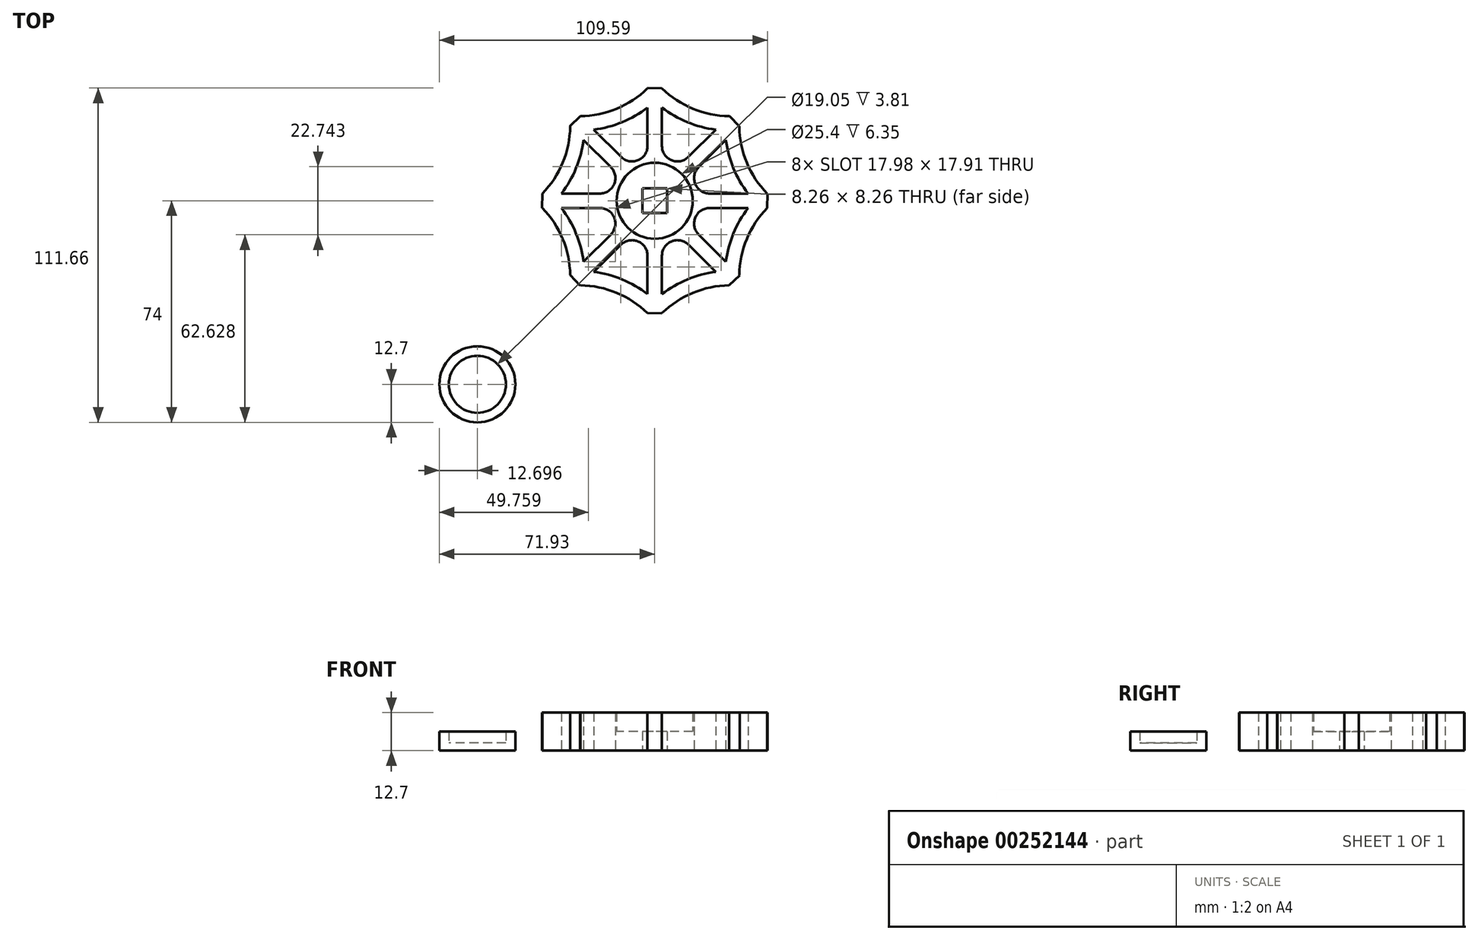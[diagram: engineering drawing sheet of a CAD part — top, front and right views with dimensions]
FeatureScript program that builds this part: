
annotation { "Feature Type Name" : "Feature", "Feature Type Description" : "" }
export const myFeature = defineFeature(function(context is Context, id is Id, definition is map)
    precondition{}
    {
        {
            var Q0;
            Q0=qCreatedBy(makeId("Top.planeOp"),FACE);
            var sketch = newSketch(context, id + "F0", { "sketchPlane" : qUnion([Q0])});
            skCircle(sketch, "E0", {"center": v(0, 0) * mm, "radius": 12.7 * mm});
            skLineSegment(sketch, "E1.0", {"start": v(18.33, -2.42) * mm, "end": v(37.66, -2.42) * mm});
            skLineSegment(sketch, "E2.0", {"start": v(18.33, 2.42) * mm, "end": v(37.66, 2.42) * mm});
            skLineSegment(sketch, "E3.trimOffspring", {"start": v(38.59, 2.42) * mm, "end": v(38.67, 2.42) * mm});
            skLineSegment(sketch, "E4.trimOffspring", {"start": v(38.59, -2.42) * mm, "end": v(38.67, -2.42) * mm});
            skLineSegment(sketch, "E5.1.0", {"start": v(11.25, 14.67) * mm, "end": v(24.92, 28.34) * mm});
            skLineSegment(sketch, "E5.1.1", {"start": v(14.67, 11.25) * mm, "end": v(28.34, 24.92) * mm});
            skLineSegment(sketch, "E5.2.0", {"start": v(-2.42, 18.33) * mm, "end": v(-2.42, 37.66) * mm});
            skLineSegment(sketch, "E5.2.1", {"start": v(2.42, 18.33) * mm, "end": v(2.42, 37.66) * mm});
            skLineSegment(sketch, "E6.3.3.0", {"start": v(-11.25, 14.67) * mm, "end": v(-24.92, 28.34) * mm});
            skLineSegment(sketch, "E6.4.3.0", {"start": v(-14.67, 11.25) * mm, "end": v(-28.34, 24.92) * mm});
            skLineSegment(sketch, "E6.3.4.0", {"start": v(-18.33, 2.42) * mm, "end": v(-37.66, 2.42) * mm});
            skLineSegment(sketch, "E6.4.4.0", {"start": v(-18.33, -2.42) * mm, "end": v(-37.66, -2.42) * mm});
            skLineSegment(sketch, "E6.3.5.0", {"start": v(-14.67, -11.25) * mm, "end": v(-28.34, -24.92) * mm});
            skLineSegment(sketch, "E6.4.5.0", {"start": v(-11.25, -14.67) * mm, "end": v(-24.92, -28.34) * mm});
            skLineSegment(sketch, "E6.3.6.0", {"start": v(-2.42, -18.33) * mm, "end": v(-2.42, -37.66) * mm});
            skLineSegment(sketch, "E6.4.6.0", {"start": v(2.42, -18.33) * mm, "end": v(2.42, -37.66) * mm});
            skLineSegment(sketch, "E6.3.7.0", {"start": v(11.25, -14.67) * mm, "end": v(24.92, -28.34) * mm});
            skLineSegment(sketch, "E6.4.7.0", {"start": v(14.67, -11.25) * mm, "end": v(28.34, -24.92) * mm});
            skLineSegment(sketch, "E7.bottom", {"start": v(4.13, 4.13) * mm, "end": v(-4.13, 4.13) * mm});
            skLineSegment(sketch, "E7.top", {"start": v(4.13, -4.13) * mm, "end": v(-4.13, -4.13) * mm});
            skLineSegment(sketch, "E7.left", {"start": v(4.13, 4.13) * mm, "end": v(4.13, -4.13) * mm});
            skLineSegment(sketch, "E7.right", {"start": v(-4.13, 4.13) * mm, "end": v(-4.13, -4.13) * mm});
            skArc(sketch, "E8.0", {"start": v(20.33, -23.74) * mm, "mid": v(10.89, -26.28) * mm, "end": v(2.42, -31.16) * mm});
            skArc(sketch, "E9.0", {"start": v(24.83, -28.25) * mm, "mid": v(12.74, -30.75) * mm, "end": v(2.42, -37.53) * mm});
            skArc(sketch, "E10.1.0", {"start": v(37.53, -2.42) * mm, "mid": v(30.75, -12.74) * mm, "end": v(28.25, -24.83) * mm});
            skArc(sketch, "E10.1.1", {"start": v(31.16, -2.42) * mm, "mid": v(26.28, -10.89) * mm, "end": v(23.74, -20.33) * mm});
            skArc(sketch, "E10.2.0", {"start": v(28.25, 24.83) * mm, "mid": v(30.75, 12.74) * mm, "end": v(37.53, 2.42) * mm});
            skArc(sketch, "E10.2.1", {"start": v(23.74, 20.33) * mm, "mid": v(26.28, 10.89) * mm, "end": v(31.16, 2.42) * mm});
            skArc(sketch, "E11.1.3.0", {"start": v(2.42, 37.53) * mm, "mid": v(12.74, 30.75) * mm, "end": v(24.83, 28.25) * mm});
            skArc(sketch, "E11.4.3.0", {"start": v(2.42, 31.16) * mm, "mid": v(10.89, 26.28) * mm, "end": v(20.33, 23.74) * mm});
            skArc(sketch, "E11.1.4.0", {"start": v(-24.83, 28.25) * mm, "mid": v(-12.74, 30.75) * mm, "end": v(-2.42, 37.53) * mm});
            skArc(sketch, "E11.4.4.0", {"start": v(-20.33, 23.74) * mm, "mid": v(-10.89, 26.28) * mm, "end": v(-2.42, 31.16) * mm});
            skArc(sketch, "E11.1.5.0", {"start": v(-37.53, 2.42) * mm, "mid": v(-30.75, 12.74) * mm, "end": v(-28.25, 24.83) * mm});
            skArc(sketch, "E11.4.5.0", {"start": v(-31.16, 2.42) * mm, "mid": v(-26.28, 10.89) * mm, "end": v(-23.74, 20.33) * mm});
            skArc(sketch, "E11.1.6.0", {"start": v(-28.25, -24.83) * mm, "mid": v(-30.75, -12.74) * mm, "end": v(-37.53, -2.42) * mm});
            skArc(sketch, "E11.4.6.0", {"start": v(-23.74, -20.33) * mm, "mid": v(-26.28, -10.89) * mm, "end": v(-31.16, -2.42) * mm});
            skArc(sketch, "E11.1.7.0", {"start": v(-2.42, -37.53) * mm, "mid": v(-12.74, -30.75) * mm, "end": v(-24.83, -28.25) * mm});
            skArc(sketch, "E11.4.7.0", {"start": v(-2.42, -31.16) * mm, "mid": v(-10.89, -26.28) * mm, "end": v(-20.33, -23.74) * mm});
            skLineSegment(sketch, "E12", {"start": v(-24.83, 28.25) * mm, "end": v(-28.34, 24.92) * mm});
            skLineSegment(sketch, "E13.1.0", {"start": v(-37.53, 2.42) * mm, "end": v(-37.66, -2.42) * mm});
            skLineSegment(sketch, "E13.2.0", {"start": v(-28.25, -24.83) * mm, "end": v(-24.92, -28.34) * mm});
            skLineSegment(sketch, "E14.2.3.0", {"start": v(-2.42, -37.53) * mm, "end": v(2.42, -37.66) * mm});
            skLineSegment(sketch, "E14.2.4.0", {"start": v(24.83, -28.25) * mm, "end": v(28.34, -24.92) * mm});
            skLineSegment(sketch, "E14.2.5.0", {"start": v(37.53, -2.42) * mm, "end": v(37.66, 2.42) * mm});
            skLineSegment(sketch, "E14.2.6.0", {"start": v(28.25, 24.83) * mm, "end": v(24.92, 28.34) * mm});
            skLineSegment(sketch, "E14.2.7.0", {"start": v(2.42, 37.53) * mm, "end": v(-2.42, 37.66) * mm});
            skArc(sketch, "E15", {"start": v(-14.67, -11.25) * mm, "mid": v(-13.55, -5.61) * mm, "end": v(-18.33, -2.42) * mm});
            skArc(sketch, "E16.1.0", {"start": v(-2.42, -18.33) * mm, "mid": v(-5.61, -13.55) * mm, "end": v(-11.25, -14.67) * mm});
            skArc(sketch, "E16.2.0", {"start": v(11.25, -14.67) * mm, "mid": v(5.61, -13.55) * mm, "end": v(2.42, -18.33) * mm});
            skArc(sketch, "E17.2.3.0", {"start": v(18.33, -2.42) * mm, "mid": v(13.55, -5.61) * mm, "end": v(14.67, -11.25) * mm});
            skArc(sketch, "E17.2.4.0", {"start": v(14.67, 11.25) * mm, "mid": v(13.55, 5.61) * mm, "end": v(18.33, 2.42) * mm});
            skArc(sketch, "E17.2.5.0", {"start": v(2.42, 18.33) * mm, "mid": v(5.61, 13.55) * mm, "end": v(11.25, 14.67) * mm});
            skArc(sketch, "E17.2.6.0", {"start": v(-11.25, 14.67) * mm, "mid": v(-5.61, 13.55) * mm, "end": v(-2.42, 18.33) * mm});
            skArc(sketch, "E17.2.7.0", {"start": v(-18.33, 2.42) * mm, "mid": v(-13.55, 5.61) * mm, "end": v(-14.67, 11.25) * mm});
            skPoint(sketch, "E18.trimOffspring.end.orphan", {"position": v(19.33, 0) * mm});
            skSolve(sketch);
        }
        {
            var Q0;
            Q0=makeQuery(id+"F0.imprint","IMPRINT",FACE,{"disambiguationData":[TD([[makeQuery(id+"F0.imprint","IMPRINT",EDGE,{"derivedFrom":sQuery(id+"F0.wireOp",EDGE,"E0")}),1.0]])]});
            extrude(context, id + "F1", {"entities" : qUnion([Q0]), "depth" : 6.35 * mm});
        }
        {
            var Q0;
            {var subQ0=sQuery(id+"F0.wireOp",EDGE,"E11.1.6.0");Q0=makeQuery(id+"F0.imprint","IMPRINT",FACE,{"disambiguationData":[TD([[makeQuery(id+"F0.imprint","IMPRINT",EDGE,{"derivedFrom":subQ0}),-1.0]])]});}
            var Q1;
            {var subQ0=sQuery(id+"F0.wireOp",EDGE,"E11.1.7.0");Q1=makeQuery(id+"F0.imprint","IMPRINT",FACE,{"disambiguationData":[TD([[makeQuery(id+"F0.imprint","IMPRINT",EDGE,{"derivedFrom":subQ0}),-1.0]])]});}
            var Q2;
            {var subQ0=sQuery(id+"F0.wireOp",EDGE,"E8.0");Q2=makeQuery(id+"F0.imprint","IMPRINT",FACE,{"disambiguationData":[TD([[makeQuery(id+"F0.imprint","IMPRINT",EDGE,{"derivedFrom":subQ0}),1.0]])]});}
            var Q3;
            {var subQ0=sQuery(id+"F0.wireOp",EDGE,"E10.1.0");Q3=makeQuery(id+"F0.imprint","IMPRINT",FACE,{"disambiguationData":[TD([[makeQuery(id+"F0.imprint","IMPRINT",EDGE,{"derivedFrom":subQ0}),-1.0]])]});}
            var Q4;
            {var subQ0=sQuery(id+"F0.wireOp",EDGE,"E10.2.0");Q4=makeQuery(id+"F0.imprint","IMPRINT",FACE,{"disambiguationData":[TD([[makeQuery(id+"F0.imprint","IMPRINT",EDGE,{"derivedFrom":subQ0}),-1.0]])]});}
            var Q5;
            Q5=makeQuery(id+"F0.imprint","IMPRINT",FACE,{"disambiguationData":[TD([[makeQuery(id+"F0.imprint","IMPRINT",EDGE,{"derivedFrom":sQuery(id+"F0.wireOp",EDGE,"E0")}),-1.0]])]});
            var Q6;
            {var subQ0=sQuery(id+"F0.wireOp",EDGE,"E11.1.5.0");Q6=makeQuery(id+"F0.imprint","IMPRINT",FACE,{"disambiguationData":[TD([[makeQuery(id+"F0.imprint","IMPRINT",EDGE,{"derivedFrom":subQ0}),-1.0]])]});}
            var Q7;
            {var subQ0=sQuery(id+"F0.wireOp",EDGE,"E11.1.4.0");Q7=makeQuery(id+"F0.imprint","IMPRINT",FACE,{"disambiguationData":[TD([[makeQuery(id+"F0.imprint","IMPRINT",EDGE,{"derivedFrom":subQ0}),-1.0]])]});}
            var Q8;
            {var subQ0=sQuery(id+"F0.wireOp",EDGE,"E11.1.3.0");Q8=makeQuery(id+"F0.imprint","IMPRINT",FACE,{"disambiguationData":[TD([[makeQuery(id+"F0.imprint","IMPRINT",EDGE,{"derivedFrom":subQ0}),-1.0]])]});}
            var Q9;
            Q9=sQuery(id+"F0.wireOp",EDGE,"E0");
            extrude(context, id + "F2", {"entities" : qUnion([Q0, Q1, Q2, Q3, Q4, Q5, Q6, Q7, Q8]), "operationType" : NewBodyOperationType.ADD, "surfaceEntities" : qUnion([Q9]), "depth" : 12.7 * mm});
        }
        {
            var Q0;
            Q0=qCreatedBy(makeId("Top.planeOp"),FACE);
            var sketch = newSketch(context, id + "F3", { "sketchPlane" : qUnion([Q0])});
            skCircle(sketch, "E19", {"center": v(-59.23, -61.3) * mm, "radius": 12.7 * mm});
            skCircle(sketch, "E20.0", {"center": v(-59.23, -61.3) * mm, "radius": 9.53 * mm});
            skSolve(sketch);
        }
        {
            var Q0;
            Q0=makeQuery(id+"F3.imprint","IMPRINT",FACE,{"disambiguationData":[TD([[makeQuery(id+"F3.imprint","IMPRINT",EDGE,{"derivedFrom":sQuery(id+"F3.wireOp",EDGE,"E19")}),1.0]])]});
            extrude(context, id + "F4", {"entities" : qUnion([Q0]), "depth" : 6.35 * mm});
        }
        {
            var Q0;
            Q0=makeQuery(id+"F3.imprint","IMPRINT",FACE,{"disambiguationData":[TD([[makeQuery(id+"F3.imprint","IMPRINT",EDGE,{"derivedFrom":sQuery(id+"F3.wireOp",EDGE,"E20.0")}),1.0]])]});
            extrude(context, id + "F5", {"entities" : qUnion([Q0]), "operationType" : NewBodyOperationType.ADD, "depth" : 2.54 * mm});
        }
    });
